# Revit family: RJ45 FTP_ENG
name_source: partatom
category: Equipement spécialisé
units: mm (PartAtom-declared; Revit-internal decimal feet)

## family parameters
Basée sur le plan de construction = Non
Cote de connecteur circulaire = Utiliser le diamètre
Couper avec des vides une fois chargée = Non
Partagée = Oui
Point de calcul de pièce = Non
Toujours verticalement = Oui
Type d'élément = Normal

## types (1)
- Connecteur RJ45 Catégorie 6 FTP (lot de 24)
    Blindé = Oui
    Catégorie = 6
    Classe ETIM = EC001121
    Couleur = IDS_GRIS
    Diamètre max du câble en entrée = 9MM
    EAN = 3414972227278
    Elévation par défaut = 0 mm  [stored 0 ft]
    Fonction = Prises murales RJ45
    Hauteur = 31 mm  [stored 0.101706 ft]
    IK = IK04
    IP = IP20
    Largeur (mm) = 18 mm  [stored 0.0590551 ft]
    Libellé BIM = Connecteur RJ45 Catégorie 6 FTP (lot de 24)
    Lien e-catalogue = https://www.legrand.fr
    Profondeur = 34 mm
    Référence Legrand = 632908
    Section AWG = 23-26
    Température de fonctionnement = -10_à_60
    Température de stockage = -10_à_70
    Type de connecteur = RJ45

note: [stored X ft] marks values corroborated as IEEE doubles in the binary element streams (Revit-internal decimal feet)
